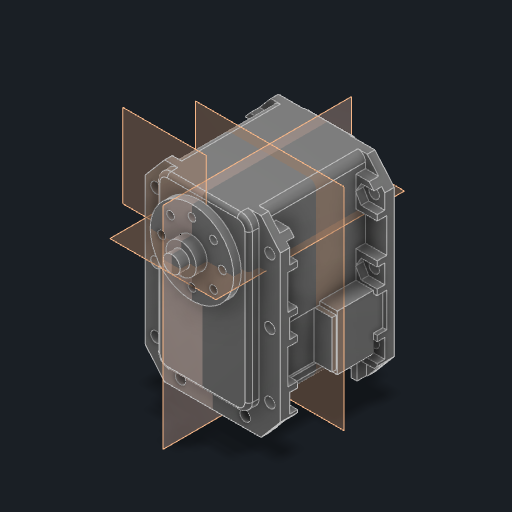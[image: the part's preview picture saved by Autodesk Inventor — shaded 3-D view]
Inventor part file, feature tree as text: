
AUTODESK INVENTOR PART (.ipt)
format: ipt  version: 2023.2 (Build 272271030, 271C)  size: 592,896 bytes
history: native  units: mm
features: other x6, extrude x4, projected_geometry x3, sketch x3
ambient origin geometry x8: Origin, YZ Plane, XZ Plane, XY Plane, X Axis, Y Axis, Z Axis, Center Point
bodies: Body1 (feature_tree)
feature tree (16):
  other  "솔리드1"
  other  "작업 평면7"
  extrude  "돌출1"  Depth=22.0mm
  extrude  "돌출2"  Depth=2.0mm TaperAngle=0.0deg
  extrude  "돌출3"  Depth=8.0mm
  extrude  "돌출4"  Depth=0.75mm TaperAngle=0.0deg
  other  "작업 평면5"
  other  "작업 평면6"
  other  "작업 평면8"
  projected_geometry  "투영된 루프1"
  sketch  "스케치2"
  projected_geometry  "투영된 루프2"
  sketch  "스케치3"
  sketch  "스케치4"
  projected_geometry  "투영된 루프3"
  other  "기준1"
